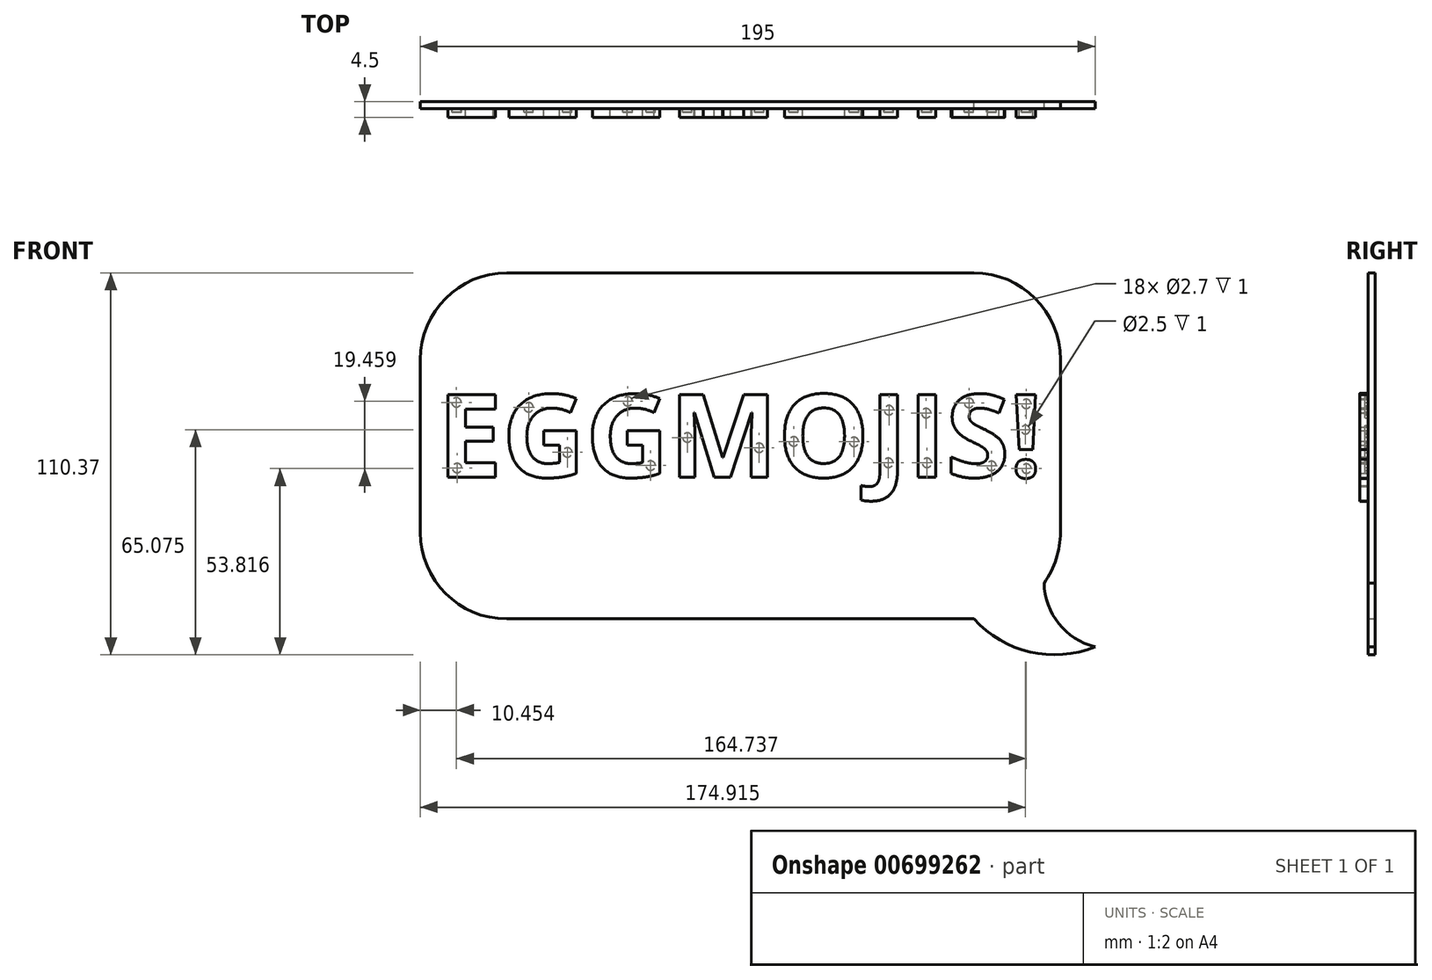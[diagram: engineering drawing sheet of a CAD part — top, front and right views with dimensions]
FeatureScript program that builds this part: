
annotation { "Feature Type Name" : "Feature", "Feature Type Description" : "" }
export const myFeature = defineFeature(function(context is Context, id is Id, definition is map)
    precondition{}
    {
        {
            var Q0;
            Q0=qCreatedBy(makeId("Front.planeOp"),FACE);
            var sketch = newSketch(context, id + "F0", { "sketchPlane" : qUnion([Q0])});
            skLineSegment(sketch, "E0.bottom", {"start": v(-109.36, 100) * mm, "end": v(75.64, 100) * mm});
            skLineSegment(sketch, "E0.top", {"start": v(-109.36, 0) * mm, "end": v(50.64, 0) * mm});
            skLineSegment(sketch, "E0.left", {"start": v(-109.36, 100) * mm, "end": v(-109.36, 0) * mm});
            skLineSegment(sketch, "E0.right", {"start": v(75.64, 100) * mm, "end": v(75.64, 25) * mm});
            skCircle(sketch, "E1", {"center": v(50.64, 25) * mm, "radius": 25 * mm});
            skArc(sketch, "E2", {"start": v(70.93, 10.4) * mm, "mid": v(75.15, -1.34) * mm, "end": v(85.64, -8.1) * mm});
            skArc(sketch, "E3", {"start": v(50.64, 0) * mm, "mid": v(66.87, -9.57) * mm, "end": v(85.64, -8.1) * mm});
            skSolve(sketch);
        }
        {
            var Q0;
            Q0=makeQuery(id+"F0.imprint","IMPRINT",FACE,{"disambiguationData":[TD([[makeQuery(id+"F0.imprint","IMPRINT",EDGE,{"derivedFrom":sQuery(id+"F0.wireOp",EDGE,"E0.bottom")}),-1.0]])]});
            var Q1;
            {var subQ0=sQuery(id+"F0.wireOp",EDGE,"E1");var subQ2=makeQuery(id+"F0.imprint","INTERSECT",VERTEX,{"derivedFrom":[sQuery(id+"F0.wireOp",EDGE,"E0.right"),subQ0]});Q1=makeQuery(id+"F0.imprint","IMPRINT",FACE,{"disambiguationData":[TD([[makeQuery(id+"F0.imprint","IMPRINT",EDGE,{"disambiguationData":[TD([[subQ2,1.0]])],"derivedFrom":subQ0}),1.0]])]});}
            var Q2;
            {var subQ2=sQuery(id+"F0.wireOp",EDGE,"E2");Q2=makeQuery(id+"F0.imprint","IMPRINT",FACE,{"disambiguationData":[TD([[makeQuery(id+"F0.imprint","IMPRINT",EDGE,{"derivedFrom":subQ2}),-1.0]])]});}
            extrude(context, id + "F1", {"entities" : qUnion([Q0, Q1, Q2]), "depth" : 2 * mm, "offsetDistance" : 25 * mm});
        }
        {
            var Q0;
            Q0=makeQuery(id+"F1.opExtrude","SWEPT_EDGE",EDGE,{"disambiguationData":[OSD([sQuery(id+"F0.wireOp",EDGE,"E0.bottom"),sQuery(id+"F0.wireOp",EDGE,"E0.right")])]});
            var Q1;
            Q1=makeQuery(id+"F1.opExtrude","SWEPT_EDGE",EDGE,{"disambiguationData":[OSD([sQuery(id+"F0.wireOp",EDGE,"E0.bottom"),sQuery(id+"F0.wireOp",EDGE,"E0.left")])]});
            var Q2;
            Q2=makeQuery(id+"F1.opExtrude","SWEPT_EDGE",EDGE,{"disambiguationData":[OSD([sQuery(id+"F0.wireOp",EDGE,"E0.top"),sQuery(id+"F0.wireOp",EDGE,"E0.left")])]});
            fillet(context, id + "F2", {"entities" : qUnion([Q0, Q1, Q2]), "radius" : 25 * mm, "tangentPropagation" : true, "allowEdgeOverflow" : false});
        }
        {
            var Q0;
            Q0=makeQuery(id+"F1.opExtrude","CAP_FACE",FACE,{"disambiguationData":[OSD([sQuery(id+"F0.wireOp",EDGE,"E0.bottom"),sQuery(id+"F0.wireOp",EDGE,"E0.top"),sQuery(id+"F0.wireOp",EDGE,"E0.left"),sQuery(id+"F0.wireOp",EDGE,"E0.right"),sQuery(id+"F0.wireOp",EDGE,"E1"),sQuery(id+"F0.wireOp",EDGE,"E2"),sQuery(id+"F0.wireOp",EDGE,"E3")])],"isStart":false});
            var sketch = newSketch(context, id + "F3", { "sketchPlane" : qUnion([Q0])});
            skText(sketch, "E4", { "text": "EGGMOJIS!", "fontName": "OpenSans-Bold.ttf"});
            skCircle(sketch, "E5", {"center": v(-11.44, 49.46) * mm, "radius": 1.25 * mm});
            skCircle(sketch, "E6", {"center": v(-32.19, 52.44) * mm, "radius": 1.25 * mm});
            skCircle(sketch, "E7", {"center": v(-49.42, 62.9) * mm, "radius": 1.25 * mm});
            skCircle(sketch, "E8", {"center": v(-98.73, 43.6) * mm, "radius": 1.25 * mm});
            skCircle(sketch, "E9", {"center": v(-78.04, 61.16) * mm, "radius": 1.25 * mm});
            skCircle(sketch, "E10", {"center": v(-98.9, 62.6) * mm, "radius": 1.25 * mm});
            skCircle(sketch, "E11", {"center": v(-66.85, 48.13) * mm, "radius": 1.25 * mm});
            skCircle(sketch, "E12", {"center": v(-42.78, 44.32) * mm, "radius": 1.25 * mm});
            skCircle(sketch, "E13", {"center": v(-1.45, 51.28) * mm, "radius": 1.25 * mm});
            skCircle(sketch, "E14", {"center": v(16, 51.17) * mm, "radius": 1.25 * mm});
            skCircle(sketch, "E15", {"center": v(26.1, 60.33) * mm, "radius": 1.25 * mm});
            skCircle(sketch, "E16", {"center": v(25.93, 45.1) * mm, "radius": 1.25 * mm});
            skCircle(sketch, "E17", {"center": v(37.08, 45.1) * mm, "radius": 1.25 * mm});
            skCircle(sketch, "E18", {"center": v(36.86, 59.45) * mm, "radius": 1.25 * mm});
            skCircle(sketch, "E19", {"center": v(49.22, 62.43) * mm, "radius": 1.25 * mm});
            skCircle(sketch, "E20", {"center": v(55.73, 44.22) * mm, "radius": 1.25 * mm});
            skCircle(sketch, "E21", {"center": v(65.83, 43.45) * mm, "radius": 1.25 * mm});
            skCircle(sketch, "E22", {"center": v(65.78, 62.16) * mm, "radius": 1.25 * mm});
            skCircle(sketch, "E23", {"center": v(65.55, 54.7) * mm, "radius": 1.25 * mm});
            skCircle(sketch, "E24", {"center": v(-98.9, 62.6) * mm, "radius": 1.35 * mm});
            skCircle(sketch, "E25", {"center": v(-78.04, 61.16) * mm, "radius": 1.35 * mm});
            skCircle(sketch, "E26", {"center": v(-49.42, 62.9) * mm, "radius": 1.35 * mm});
            skCircle(sketch, "E27", {"center": v(-66.85, 48.13) * mm, "radius": 1.35 * mm});
            skCircle(sketch, "E28", {"center": v(-98.73, 43.6) * mm, "radius": 1.35 * mm});
            skCircle(sketch, "E29", {"center": v(-32.19, 52.44) * mm, "radius": 1.35 * mm});
            skCircle(sketch, "E30", {"center": v(-42.78, 44.32) * mm, "radius": 1.35 * mm});
            skCircle(sketch, "E31", {"center": v(-11.44, 49.46) * mm, "radius": 1.35 * mm});
            skCircle(sketch, "E32", {"center": v(-1.45, 51.28) * mm, "radius": 1.35 * mm});
            skCircle(sketch, "E33", {"center": v(16, 51.17) * mm, "radius": 1.35 * mm});
            skCircle(sketch, "E34", {"center": v(26.1, 60.33) * mm, "radius": 1.35 * mm});
            skCircle(sketch, "E35", {"center": v(37.08, 45.1) * mm, "radius": 1.35 * mm});
            skCircle(sketch, "E36", {"center": v(36.86, 59.45) * mm, "radius": 1.35 * mm});
            skCircle(sketch, "E37", {"center": v(49.22, 62.43) * mm, "radius": 1.35 * mm});
            skCircle(sketch, "E38", {"center": v(55.73, 44.22) * mm, "radius": 1.35 * mm});
            skCircle(sketch, "E39", {"center": v(65.83, 43.45) * mm, "radius": 1.35 * mm});
            skCircle(sketch, "E40", {"center": v(65.55, 54.7) * mm, "radius": 1.35 * mm});
            skCircle(sketch, "E41", {"center": v(65.78, 62.16) * mm, "radius": 1.35 * mm});
            skCircle(sketch, "E42", {"center": v(25.93, 45.1) * mm, "radius": 1.35 * mm});
            const initialGuessF3  = {"E4": [-0.10436, 0.04101, 1, 0, 0.02399]};
            skSetInitialGuess(sketch, initialGuessF3);
            skSolve(sketch);
        }
        {
            var Q0;
            Q0 = qSketchRegion(id + "F3", true);
            var Q1;
            Q1=makeQuery(id+"F3.imprint","IMPRINT",FACE,{"disambiguationData":[TD([[makeQuery(id+"F3.imprint","IMPRINT",EDGE,{"derivedFrom":sQuery(id+"F3.wireOp",EDGE,"E5")}),1.0]])]});
            var Q2;
            Q2=makeQuery(id+"F3.imprint","IMPRINT",FACE,{"disambiguationData":[TD([[makeQuery(id+"F3.imprint","IMPRINT",EDGE,{"derivedFrom":sQuery(id+"F3.wireOp",EDGE,"E5")}),-1.0]])]});
            var Q3;
            Q3=makeQuery(id+"F3.imprint","IMPRINT",FACE,{"disambiguationData":[TD([[makeQuery(id+"F3.imprint","IMPRINT",EDGE,{"derivedFrom":sQuery(id+"F3.wireOp",EDGE,"E6")}),1.0]])]});
            var Q4;
            Q4=makeQuery(id+"F3.imprint","IMPRINT",FACE,{"disambiguationData":[TD([[makeQuery(id+"F3.imprint","IMPRINT",EDGE,{"derivedFrom":sQuery(id+"F3.wireOp",EDGE,"E6")}),-1.0]])]});
            var Q5;
            Q5=makeQuery(id+"F3.imprint","IMPRINT",FACE,{"disambiguationData":[TD([[makeQuery(id+"F3.imprint","IMPRINT",EDGE,{"derivedFrom":sQuery(id+"F3.wireOp",EDGE,"E12")}),-1.0]])]});
            var Q6;
            Q6=makeQuery(id+"F3.imprint","IMPRINT",FACE,{"disambiguationData":[TD([[makeQuery(id+"F3.imprint","IMPRINT",EDGE,{"derivedFrom":sQuery(id+"F3.wireOp",EDGE,"E12")}),1.0]])]});
            var Q7;
            Q7=makeQuery(id+"F3.imprint","IMPRINT",FACE,{"disambiguationData":[TD([[makeQuery(id+"F3.imprint","IMPRINT",EDGE,{"derivedFrom":sQuery(id+"F3.wireOp",EDGE,"E7")}),1.0]])]});
            var Q8;
            Q8=makeQuery(id+"F3.imprint","IMPRINT",FACE,{"disambiguationData":[TD([[makeQuery(id+"F3.imprint","IMPRINT",EDGE,{"derivedFrom":sQuery(id+"F3.wireOp",EDGE,"E7")}),-1.0]])]});
            var Q9;
            Q9=makeQuery(id+"F3.imprint","IMPRINT",FACE,{"disambiguationData":[TD([[makeQuery(id+"F3.imprint","IMPRINT",EDGE,{"derivedFrom":sQuery(id+"F3.wireOp",EDGE,"E9")}),1.0]])]});
            var Q10;
            Q10=makeQuery(id+"F3.imprint","IMPRINT",FACE,{"disambiguationData":[TD([[makeQuery(id+"F3.imprint","IMPRINT",EDGE,{"derivedFrom":sQuery(id+"F3.wireOp",EDGE,"E9")}),-1.0]])]});
            var Q11;
            Q11=makeQuery(id+"F3.imprint","IMPRINT",FACE,{"disambiguationData":[TD([[makeQuery(id+"F3.imprint","IMPRINT",EDGE,{"derivedFrom":sQuery(id+"F3.wireOp",EDGE,"E11")}),1.0]])]});
            var Q12;
            Q12=makeQuery(id+"F3.imprint","IMPRINT",FACE,{"disambiguationData":[TD([[makeQuery(id+"F3.imprint","IMPRINT",EDGE,{"derivedFrom":sQuery(id+"F3.wireOp",EDGE,"E11")}),-1.0]])]});
            var Q13;
            Q13=makeQuery(id+"F3.imprint","IMPRINT",FACE,{"disambiguationData":[TD([[makeQuery(id+"F3.imprint","IMPRINT",EDGE,{"derivedFrom":sQuery(id+"F3.wireOp",EDGE,"E10")}),1.0]])]});
            var Q14;
            Q14=makeQuery(id+"F3.imprint","IMPRINT",FACE,{"disambiguationData":[TD([[makeQuery(id+"F3.imprint","IMPRINT",EDGE,{"derivedFrom":sQuery(id+"F3.wireOp",EDGE,"E10")}),-1.0]])]});
            var Q15;
            Q15=makeQuery(id+"F3.imprint","IMPRINT",FACE,{"disambiguationData":[TD([[makeQuery(id+"F3.imprint","IMPRINT",EDGE,{"derivedFrom":sQuery(id+"F3.wireOp",EDGE,"E8")}),1.0]])]});
            var Q16;
            Q16=makeQuery(id+"F3.imprint","IMPRINT",FACE,{"disambiguationData":[TD([[makeQuery(id+"F3.imprint","IMPRINT",EDGE,{"derivedFrom":sQuery(id+"F3.wireOp",EDGE,"E8")}),-1.0]])]});
            var Q17;
            Q17=makeQuery(id+"F3.imprint","IMPRINT",FACE,{"disambiguationData":[TD([[makeQuery(id+"F3.imprint","IMPRINT",EDGE,{"derivedFrom":sQuery(id+"F3.wireOp",EDGE,"E13")}),1.0]])]});
            var Q18;
            Q18=makeQuery(id+"F3.imprint","IMPRINT",FACE,{"disambiguationData":[TD([[makeQuery(id+"F3.imprint","IMPRINT",EDGE,{"derivedFrom":sQuery(id+"F3.wireOp",EDGE,"E13")}),-1.0]])]});
            var Q19;
            Q19=makeQuery(id+"F3.imprint","IMPRINT",FACE,{"disambiguationData":[TD([[makeQuery(id+"F3.imprint","IMPRINT",EDGE,{"derivedFrom":sQuery(id+"F3.wireOp",EDGE,"E14")}),1.0]])]});
            var Q20;
            Q20=makeQuery(id+"F3.imprint","IMPRINT",FACE,{"disambiguationData":[TD([[makeQuery(id+"F3.imprint","IMPRINT",EDGE,{"derivedFrom":sQuery(id+"F3.wireOp",EDGE,"E14")}),-1.0]])]});
            var Q21;
            Q21=makeQuery(id+"F3.imprint","IMPRINT",FACE,{"disambiguationData":[TD([[makeQuery(id+"F3.imprint","IMPRINT",EDGE,{"derivedFrom":sQuery(id+"F3.wireOp",EDGE,"E16")}),1.0]])]});
            var Q22;
            Q22=makeQuery(id+"F3.imprint","IMPRINT",FACE,{"disambiguationData":[TD([[makeQuery(id+"F3.imprint","IMPRINT",EDGE,{"derivedFrom":sQuery(id+"F3.wireOp",EDGE,"E16")}),-1.0]])]});
            var Q23;
            Q23=makeQuery(id+"F3.imprint","IMPRINT",FACE,{"disambiguationData":[TD([[makeQuery(id+"F3.imprint","IMPRINT",EDGE,{"derivedFrom":sQuery(id+"F3.wireOp",EDGE,"E15")}),1.0]])]});
            var Q24;
            Q24=makeQuery(id+"F3.imprint","IMPRINT",FACE,{"disambiguationData":[TD([[makeQuery(id+"F3.imprint","IMPRINT",EDGE,{"derivedFrom":sQuery(id+"F3.wireOp",EDGE,"E15")}),-1.0]])]});
            var Q25;
            Q25=makeQuery(id+"F3.imprint","IMPRINT",FACE,{"disambiguationData":[TD([[makeQuery(id+"F3.imprint","IMPRINT",EDGE,{"derivedFrom":sQuery(id+"F3.wireOp",EDGE,"E18")}),1.0]])]});
            var Q26;
            Q26=makeQuery(id+"F3.imprint","IMPRINT",FACE,{"disambiguationData":[TD([[makeQuery(id+"F3.imprint","IMPRINT",EDGE,{"derivedFrom":sQuery(id+"F3.wireOp",EDGE,"E18")}),-1.0]])]});
            var Q27;
            Q27=makeQuery(id+"F3.imprint","IMPRINT",FACE,{"disambiguationData":[TD([[makeQuery(id+"F3.imprint","IMPRINT",EDGE,{"derivedFrom":sQuery(id+"F3.wireOp",EDGE,"E17")}),1.0]])]});
            var Q28;
            Q28=makeQuery(id+"F3.imprint","IMPRINT",FACE,{"disambiguationData":[TD([[makeQuery(id+"F3.imprint","IMPRINT",EDGE,{"derivedFrom":sQuery(id+"F3.wireOp",EDGE,"E17")}),-1.0]])]});
            var Q29;
            Q29=makeQuery(id+"F3.imprint","IMPRINT",FACE,{"disambiguationData":[TD([[makeQuery(id+"F3.imprint","IMPRINT",EDGE,{"derivedFrom":sQuery(id+"F3.wireOp",EDGE,"E20")}),1.0]])]});
            var Q30;
            Q30=makeQuery(id+"F3.imprint","IMPRINT",FACE,{"disambiguationData":[TD([[makeQuery(id+"F3.imprint","IMPRINT",EDGE,{"derivedFrom":sQuery(id+"F3.wireOp",EDGE,"E20")}),-1.0]])]});
            var Q31;
            Q31=makeQuery(id+"F3.imprint","IMPRINT",FACE,{"disambiguationData":[TD([[makeQuery(id+"F3.imprint","IMPRINT",EDGE,{"derivedFrom":sQuery(id+"F3.wireOp",EDGE,"E19")}),1.0]])]});
            var Q32;
            Q32=makeQuery(id+"F3.imprint","IMPRINT",FACE,{"disambiguationData":[TD([[makeQuery(id+"F3.imprint","IMPRINT",EDGE,{"derivedFrom":sQuery(id+"F3.wireOp",EDGE,"E19")}),-1.0]])]});
            var Q33;
            Q33=makeQuery(id+"F3.imprint","IMPRINT",FACE,{"disambiguationData":[TD([[makeQuery(id+"F3.imprint","IMPRINT",EDGE,{"derivedFrom":sQuery(id+"F3.wireOp",EDGE,"E22")}),1.0]])]});
            var Q34;
            Q34=makeQuery(id+"F3.imprint","IMPRINT",FACE,{"disambiguationData":[TD([[makeQuery(id+"F3.imprint","IMPRINT",EDGE,{"derivedFrom":sQuery(id+"F3.wireOp",EDGE,"E22")}),-1.0]])]});
            var Q35;
            Q35=makeQuery(id+"F3.imprint","IMPRINT",FACE,{"disambiguationData":[TD([[makeQuery(id+"F3.imprint","IMPRINT",EDGE,{"derivedFrom":sQuery(id+"F3.wireOp",EDGE,"E23")}),1.0]])]});
            var Q36;
            Q36=makeQuery(id+"F3.imprint","IMPRINT",FACE,{"disambiguationData":[TD([[makeQuery(id+"F3.imprint","IMPRINT",EDGE,{"derivedFrom":sQuery(id+"F3.wireOp",EDGE,"E23")}),-1.0]])]});
            var Q37;
            Q37=makeQuery(id+"F3.imprint","IMPRINT",FACE,{"disambiguationData":[TD([[makeQuery(id+"F3.imprint","IMPRINT",EDGE,{"derivedFrom":sQuery(id+"F3.wireOp",EDGE,"E21")}),1.0]])]});
            var Q38;
            Q38=makeQuery(id+"F3.imprint","IMPRINT",FACE,{"disambiguationData":[TD([[makeQuery(id+"F3.imprint","IMPRINT",EDGE,{"derivedFrom":sQuery(id+"F3.wireOp",EDGE,"E21")}),-1.0]])]});
            extrude(context, id + "F4", {"entities" : qUnion([Q0, Q1, Q2, Q3, Q4, Q5, Q6, Q7, Q8, Q9, Q10, Q11, Q12, Q13, Q14, Q15, Q16, Q17, Q18, Q19, Q20, Q21, Q22, Q23, Q24, Q25, Q26, Q27, Q28, Q29, Q30, Q31, Q32, Q33, Q34, Q35, Q36, Q37, Q38]), "depth" : 2.5 * mm, "offsetDistance" : 25 * mm});
        }
        {
            var Q0;
            Q0=makeQuery(id+"F3.imprint","IMPRINT",FACE,{"disambiguationData":[TD([[makeQuery(id+"F3.imprint","IMPRINT",EDGE,{"derivedFrom":sQuery(id+"F3.wireOp",EDGE,"E8")}),1.0]])]});
            var Q1;
            Q1=makeQuery(id+"F3.imprint","IMPRINT",FACE,{"disambiguationData":[TD([[makeQuery(id+"F3.imprint","IMPRINT",EDGE,{"derivedFrom":sQuery(id+"F3.wireOp",EDGE,"E10")}),1.0]])]});
            var Q2;
            Q2=makeQuery(id+"F3.imprint","IMPRINT",FACE,{"disambiguationData":[TD([[makeQuery(id+"F3.imprint","IMPRINT",EDGE,{"derivedFrom":sQuery(id+"F3.wireOp",EDGE,"E9")}),1.0]])]});
            var Q3;
            Q3=makeQuery(id+"F3.imprint","IMPRINT",FACE,{"disambiguationData":[TD([[makeQuery(id+"F3.imprint","IMPRINT",EDGE,{"derivedFrom":sQuery(id+"F3.wireOp",EDGE,"E11")}),1.0]])]});
            var Q4;
            Q4=makeQuery(id+"F3.imprint","IMPRINT",FACE,{"disambiguationData":[TD([[makeQuery(id+"F3.imprint","IMPRINT",EDGE,{"derivedFrom":sQuery(id+"F3.wireOp",EDGE,"E7")}),1.0]])]});
            var Q5;
            Q5=makeQuery(id+"F3.imprint","IMPRINT",FACE,{"disambiguationData":[TD([[makeQuery(id+"F3.imprint","IMPRINT",EDGE,{"derivedFrom":sQuery(id+"F3.wireOp",EDGE,"E12")}),1.0]])]});
            var Q6;
            Q6=makeQuery(id+"F3.imprint","IMPRINT",FACE,{"disambiguationData":[TD([[makeQuery(id+"F3.imprint","IMPRINT",EDGE,{"derivedFrom":sQuery(id+"F3.wireOp",EDGE,"E6")}),1.0]])]});
            var Q7;
            Q7=makeQuery(id+"F3.imprint","IMPRINT",FACE,{"disambiguationData":[TD([[makeQuery(id+"F3.imprint","IMPRINT",EDGE,{"derivedFrom":sQuery(id+"F3.wireOp",EDGE,"E5")}),1.0]])]});
            var Q8;
            Q8=makeQuery(id+"F3.imprint","IMPRINT",FACE,{"disambiguationData":[TD([[makeQuery(id+"F3.imprint","IMPRINT",EDGE,{"derivedFrom":sQuery(id+"F3.wireOp",EDGE,"E13")}),1.0]])]});
            var Q9;
            Q9=makeQuery(id+"F3.imprint","IMPRINT",FACE,{"disambiguationData":[TD([[makeQuery(id+"F3.imprint","IMPRINT",EDGE,{"derivedFrom":sQuery(id+"F3.wireOp",EDGE,"E14")}),1.0]])]});
            var Q10;
            Q10=makeQuery(id+"F3.imprint","IMPRINT",FACE,{"disambiguationData":[TD([[makeQuery(id+"F3.imprint","IMPRINT",EDGE,{"derivedFrom":sQuery(id+"F3.wireOp",EDGE,"E16")}),1.0]])]});
            var Q11;
            Q11=makeQuery(id+"F3.imprint","IMPRINT",FACE,{"disambiguationData":[TD([[makeQuery(id+"F3.imprint","IMPRINT",EDGE,{"derivedFrom":sQuery(id+"F3.wireOp",EDGE,"E15")}),1.0]])]});
            var Q12;
            Q12=makeQuery(id+"F3.imprint","IMPRINT",FACE,{"disambiguationData":[TD([[makeQuery(id+"F3.imprint","IMPRINT",EDGE,{"derivedFrom":sQuery(id+"F3.wireOp",EDGE,"E18")}),1.0]])]});
            var Q13;
            Q13=makeQuery(id+"F3.imprint","IMPRINT",FACE,{"disambiguationData":[TD([[makeQuery(id+"F3.imprint","IMPRINT",EDGE,{"derivedFrom":sQuery(id+"F3.wireOp",EDGE,"E17")}),1.0]])]});
            var Q14;
            Q14=makeQuery(id+"F3.imprint","IMPRINT",FACE,{"disambiguationData":[TD([[makeQuery(id+"F3.imprint","IMPRINT",EDGE,{"derivedFrom":sQuery(id+"F3.wireOp",EDGE,"E20")}),1.0]])]});
            var Q15;
            Q15=makeQuery(id+"F3.imprint","IMPRINT",FACE,{"disambiguationData":[TD([[makeQuery(id+"F3.imprint","IMPRINT",EDGE,{"derivedFrom":sQuery(id+"F3.wireOp",EDGE,"E19")}),1.0]])]});
            var Q16;
            Q16=makeQuery(id+"F3.imprint","IMPRINT",FACE,{"disambiguationData":[TD([[makeQuery(id+"F3.imprint","IMPRINT",EDGE,{"derivedFrom":sQuery(id+"F3.wireOp",EDGE,"E22")}),1.0]])]});
            var Q17;
            Q17=makeQuery(id+"F3.imprint","IMPRINT",FACE,{"disambiguationData":[TD([[makeQuery(id+"F3.imprint","IMPRINT",EDGE,{"derivedFrom":sQuery(id+"F3.wireOp",EDGE,"E23")}),1.0]])]});
            var Q18;
            Q18=makeQuery(id+"F3.imprint","IMPRINT",FACE,{"disambiguationData":[TD([[makeQuery(id+"F3.imprint","IMPRINT",EDGE,{"derivedFrom":sQuery(id+"F3.wireOp",EDGE,"E21")}),1.0]])]});
            extrude(context, id + "F5", {"entities" : qUnion([Q0, Q1, Q2, Q3, Q4, Q5, Q6, Q7, Q8, Q9, Q10, Q11, Q12, Q13, Q14, Q15, Q16, Q17, Q18]), "operationType" : NewBodyOperationType.ADD, "depth" : 0.5 * mm, "offsetDistance" : 25 * mm, "hasDraft" : true, "draftAngle" : 3 * degree, "draftPullDirection" : true});
        }
        {
            var Q0;
            Q0=makeQuery(id+"F3.imprint","IMPRINT",FACE,{"disambiguationData":[TD([[makeQuery(id+"F3.imprint","IMPRINT",EDGE,{"derivedFrom":sQuery(id+"F3.wireOp",EDGE,"E8")}),-1.0]])]});
            var Q1;
            Q1=makeQuery(id+"F3.imprint","IMPRINT",FACE,{"disambiguationData":[TD([[makeQuery(id+"F3.imprint","IMPRINT",EDGE,{"derivedFrom":sQuery(id+"F3.wireOp",EDGE,"E8")}),1.0]])]});
            var Q2;
            Q2=makeQuery(id+"F3.imprint","IMPRINT",FACE,{"disambiguationData":[TD([[makeQuery(id+"F3.imprint","IMPRINT",EDGE,{"derivedFrom":sQuery(id+"F3.wireOp",EDGE,"E10")}),-1.0]])]});
            var Q3;
            Q3=makeQuery(id+"F3.imprint","IMPRINT",FACE,{"disambiguationData":[TD([[makeQuery(id+"F3.imprint","IMPRINT",EDGE,{"derivedFrom":sQuery(id+"F3.wireOp",EDGE,"E10")}),1.0]])]});
            var Q4;
            Q4=makeQuery(id+"F3.imprint","IMPRINT",FACE,{"disambiguationData":[TD([[makeQuery(id+"F3.imprint","IMPRINT",EDGE,{"derivedFrom":sQuery(id+"F3.wireOp",EDGE,"E9")}),-1.0]])]});
            var Q5;
            Q5=makeQuery(id+"F3.imprint","IMPRINT",FACE,{"disambiguationData":[TD([[makeQuery(id+"F3.imprint","IMPRINT",EDGE,{"derivedFrom":sQuery(id+"F3.wireOp",EDGE,"E9")}),1.0]])]});
            var Q6;
            Q6=makeQuery(id+"F3.imprint","IMPRINT",FACE,{"disambiguationData":[TD([[makeQuery(id+"F3.imprint","IMPRINT",EDGE,{"derivedFrom":sQuery(id+"F3.wireOp",EDGE,"E11")}),-1.0]])]});
            var Q7;
            Q7=makeQuery(id+"F3.imprint","IMPRINT",FACE,{"disambiguationData":[TD([[makeQuery(id+"F3.imprint","IMPRINT",EDGE,{"derivedFrom":sQuery(id+"F3.wireOp",EDGE,"E11")}),1.0]])]});
            var Q8;
            Q8=makeQuery(id+"F3.imprint","IMPRINT",FACE,{"disambiguationData":[TD([[makeQuery(id+"F3.imprint","IMPRINT",EDGE,{"derivedFrom":sQuery(id+"F3.wireOp",EDGE,"E12")}),-1.0]])]});
            var Q9;
            Q9=makeQuery(id+"F3.imprint","IMPRINT",FACE,{"disambiguationData":[TD([[makeQuery(id+"F3.imprint","IMPRINT",EDGE,{"derivedFrom":sQuery(id+"F3.wireOp",EDGE,"E12")}),1.0]])]});
            var Q10;
            Q10=makeQuery(id+"F3.imprint","IMPRINT",FACE,{"disambiguationData":[TD([[makeQuery(id+"F3.imprint","IMPRINT",EDGE,{"derivedFrom":sQuery(id+"F3.wireOp",EDGE,"E7")}),-1.0]])]});
            var Q11;
            Q11=makeQuery(id+"F3.imprint","IMPRINT",FACE,{"disambiguationData":[TD([[makeQuery(id+"F3.imprint","IMPRINT",EDGE,{"derivedFrom":sQuery(id+"F3.wireOp",EDGE,"E7")}),1.0]])]});
            var Q12;
            Q12=makeQuery(id+"F3.imprint","IMPRINT",FACE,{"disambiguationData":[TD([[makeQuery(id+"F3.imprint","IMPRINT",EDGE,{"derivedFrom":sQuery(id+"F3.wireOp",EDGE,"E6")}),-1.0]])]});
            var Q13;
            Q13=makeQuery(id+"F3.imprint","IMPRINT",FACE,{"disambiguationData":[TD([[makeQuery(id+"F3.imprint","IMPRINT",EDGE,{"derivedFrom":sQuery(id+"F3.wireOp",EDGE,"E6")}),1.0]])]});
            var Q14;
            Q14=makeQuery(id+"F3.imprint","IMPRINT",FACE,{"disambiguationData":[TD([[makeQuery(id+"F3.imprint","IMPRINT",EDGE,{"derivedFrom":sQuery(id+"F3.wireOp",EDGE,"E5")}),-1.0]])]});
            var Q15;
            Q15=makeQuery(id+"F3.imprint","IMPRINT",FACE,{"disambiguationData":[TD([[makeQuery(id+"F3.imprint","IMPRINT",EDGE,{"derivedFrom":sQuery(id+"F3.wireOp",EDGE,"E5")}),1.0]])]});
            var Q16;
            Q16=makeQuery(id+"F3.imprint","IMPRINT",FACE,{"disambiguationData":[TD([[makeQuery(id+"F3.imprint","IMPRINT",EDGE,{"derivedFrom":sQuery(id+"F3.wireOp",EDGE,"E13")}),-1.0]])]});
            var Q17;
            Q17=makeQuery(id+"F3.imprint","IMPRINT",FACE,{"disambiguationData":[TD([[makeQuery(id+"F3.imprint","IMPRINT",EDGE,{"derivedFrom":sQuery(id+"F3.wireOp",EDGE,"E13")}),1.0]])]});
            var Q18;
            Q18=makeQuery(id+"F3.imprint","IMPRINT",FACE,{"disambiguationData":[TD([[makeQuery(id+"F3.imprint","IMPRINT",EDGE,{"derivedFrom":sQuery(id+"F3.wireOp",EDGE,"E14")}),-1.0]])]});
            var Q19;
            Q19=makeQuery(id+"F3.imprint","IMPRINT",FACE,{"disambiguationData":[TD([[makeQuery(id+"F3.imprint","IMPRINT",EDGE,{"derivedFrom":sQuery(id+"F3.wireOp",EDGE,"E14")}),1.0]])]});
            var Q20;
            Q20=makeQuery(id+"F3.imprint","IMPRINT",FACE,{"disambiguationData":[TD([[makeQuery(id+"F3.imprint","IMPRINT",EDGE,{"derivedFrom":sQuery(id+"F3.wireOp",EDGE,"E16")}),-1.0]])]});
            var Q21;
            Q21=makeQuery(id+"F3.imprint","IMPRINT",FACE,{"disambiguationData":[TD([[makeQuery(id+"F3.imprint","IMPRINT",EDGE,{"derivedFrom":sQuery(id+"F3.wireOp",EDGE,"E16")}),1.0]])]});
            var Q22;
            Q22=makeQuery(id+"F3.imprint","IMPRINT",FACE,{"disambiguationData":[TD([[makeQuery(id+"F3.imprint","IMPRINT",EDGE,{"derivedFrom":sQuery(id+"F3.wireOp",EDGE,"E17")}),-1.0]])]});
            var Q23;
            Q23=makeQuery(id+"F3.imprint","IMPRINT",FACE,{"disambiguationData":[TD([[makeQuery(id+"F3.imprint","IMPRINT",EDGE,{"derivedFrom":sQuery(id+"F3.wireOp",EDGE,"E17")}),1.0]])]});
            var Q24;
            Q24=makeQuery(id+"F3.imprint","IMPRINT",FACE,{"disambiguationData":[TD([[makeQuery(id+"F3.imprint","IMPRINT",EDGE,{"derivedFrom":sQuery(id+"F3.wireOp",EDGE,"E15")}),-1.0]])]});
            var Q25;
            Q25=makeQuery(id+"F3.imprint","IMPRINT",FACE,{"disambiguationData":[TD([[makeQuery(id+"F3.imprint","IMPRINT",EDGE,{"derivedFrom":sQuery(id+"F3.wireOp",EDGE,"E15")}),1.0]])]});
            var Q26;
            Q26=makeQuery(id+"F3.imprint","IMPRINT",FACE,{"disambiguationData":[TD([[makeQuery(id+"F3.imprint","IMPRINT",EDGE,{"derivedFrom":sQuery(id+"F3.wireOp",EDGE,"E18")}),-1.0]])]});
            var Q27;
            Q27=makeQuery(id+"F3.imprint","IMPRINT",FACE,{"disambiguationData":[TD([[makeQuery(id+"F3.imprint","IMPRINT",EDGE,{"derivedFrom":sQuery(id+"F3.wireOp",EDGE,"E18")}),1.0]])]});
            var Q28;
            Q28=makeQuery(id+"F3.imprint","IMPRINT",FACE,{"disambiguationData":[TD([[makeQuery(id+"F3.imprint","IMPRINT",EDGE,{"derivedFrom":sQuery(id+"F3.wireOp",EDGE,"E19")}),-1.0]])]});
            var Q29;
            Q29=makeQuery(id+"F3.imprint","IMPRINT",FACE,{"disambiguationData":[TD([[makeQuery(id+"F3.imprint","IMPRINT",EDGE,{"derivedFrom":sQuery(id+"F3.wireOp",EDGE,"E19")}),1.0]])]});
            var Q30;
            Q30=makeQuery(id+"F3.imprint","IMPRINT",FACE,{"disambiguationData":[TD([[makeQuery(id+"F3.imprint","IMPRINT",EDGE,{"derivedFrom":sQuery(id+"F3.wireOp",EDGE,"E20")}),-1.0]])]});
            var Q31;
            Q31=makeQuery(id+"F3.imprint","IMPRINT",FACE,{"disambiguationData":[TD([[makeQuery(id+"F3.imprint","IMPRINT",EDGE,{"derivedFrom":sQuery(id+"F3.wireOp",EDGE,"E20")}),1.0]])]});
            var Q32;
            Q32=makeQuery(id+"F3.imprint","IMPRINT",FACE,{"disambiguationData":[TD([[makeQuery(id+"F3.imprint","IMPRINT",EDGE,{"derivedFrom":sQuery(id+"F3.wireOp",EDGE,"E21")}),-1.0]])]});
            var Q33;
            Q33=makeQuery(id+"F3.imprint","IMPRINT",FACE,{"disambiguationData":[TD([[makeQuery(id+"F3.imprint","IMPRINT",EDGE,{"derivedFrom":sQuery(id+"F3.wireOp",EDGE,"E21")}),1.0]])]});
            var Q34;
            Q34=makeQuery(id+"F3.imprint","IMPRINT",FACE,{"disambiguationData":[TD([[makeQuery(id+"F3.imprint","IMPRINT",EDGE,{"derivedFrom":sQuery(id+"F3.wireOp",EDGE,"E23")}),1.0]])]});
            var Q35;
            Q35=makeQuery(id+"F3.imprint","IMPRINT",FACE,{"disambiguationData":[TD([[makeQuery(id+"F3.imprint","IMPRINT",EDGE,{"derivedFrom":sQuery(id+"F3.wireOp",EDGE,"E22")}),-1.0]])]});
            var Q36;
            Q36=makeQuery(id+"F3.imprint","IMPRINT",FACE,{"disambiguationData":[TD([[makeQuery(id+"F3.imprint","IMPRINT",EDGE,{"derivedFrom":sQuery(id+"F3.wireOp",EDGE,"E22")}),1.0]])]});
            extrude(context, id + "F6", {"entities" : qUnion([Q0, Q1, Q2, Q3, Q4, Q5, Q6, Q7, Q8, Q9, Q10, Q11, Q12, Q13, Q14, Q15, Q16, Q17, Q18, Q19, Q20, Q21, Q22, Q23, Q24, Q25, Q26, Q27, Q28, Q29, Q30, Q31, Q32, Q33, Q34, Q35, Q36]), "operationType" : NewBodyOperationType.REMOVE, "depth" : 1 * mm, "offsetDistance" : 25 * mm});
        }
    });
